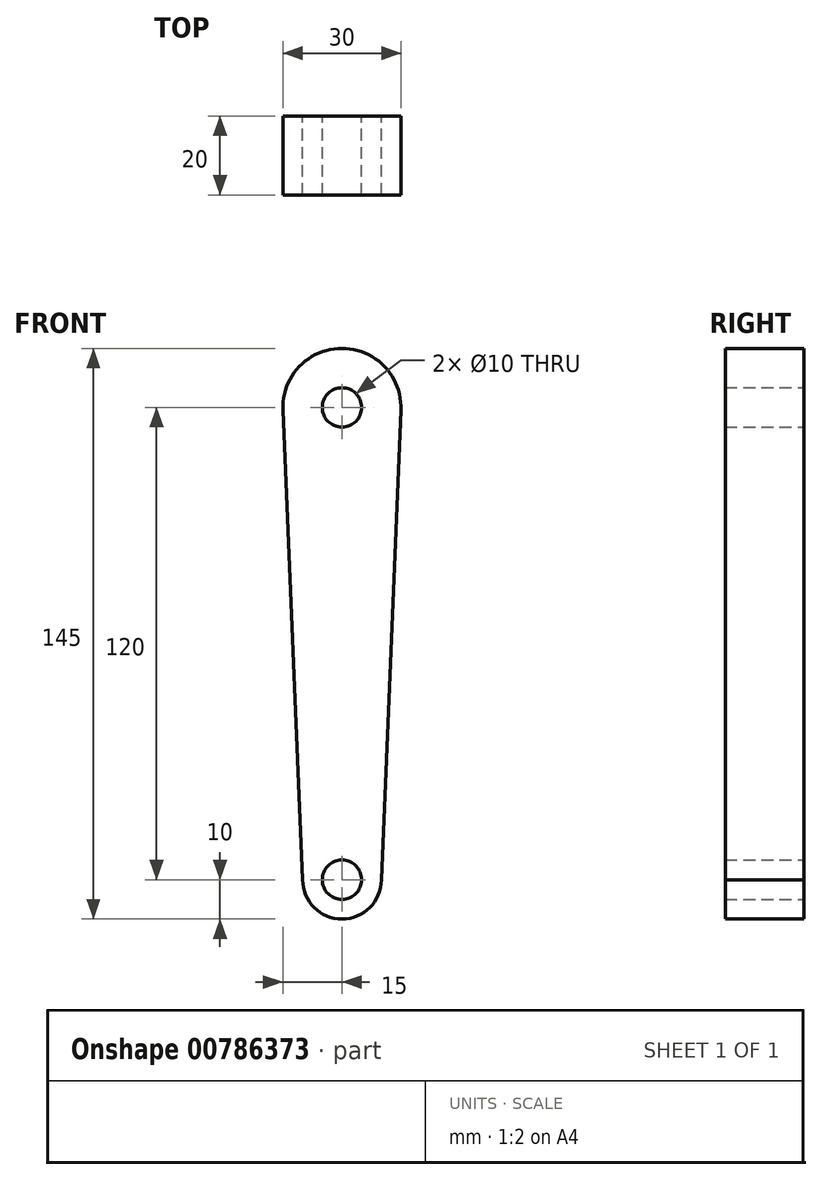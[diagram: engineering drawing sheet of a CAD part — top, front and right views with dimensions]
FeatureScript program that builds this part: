
annotation { "Feature Type Name" : "Feature", "Feature Type Description" : "" }
export const myFeature = defineFeature(function(context is Context, id is Id, definition is map)
    precondition{}
    {
        {
            var Q0;
            Q0=qCreatedBy(makeId("Front.planeOp"),FACE);
            var sketch = newSketch(context, id + "F0", { "sketchPlane" : qUnion([Q0])});
            skCircle(sketch, "E0", {"center": v(0, 0) * mm, "radius": 15 * mm});
            skCircle(sketch, "E1.0", {"center": v(0, 0) * mm, "radius": 5 * mm});
            skCircle(sketch, "E2", {"center": v(0, -120) * mm, "radius": 10 * mm});
            skLineSegment(sketch, "E3", {"start": v(-10, -120) * mm, "end": v(-14.99, -0.63) * mm});
            skLineSegment(sketch, "E4", {"start": v(10, -120) * mm, "end": v(14.99, -0.63) * mm});
            skCircle(sketch, "E5.0", {"center": v(0, -120) * mm, "radius": 5 * mm});
            skSolve(sketch);
        }
        {
            var Q0;
            {var subQ0=sQuery(id+"F0.wireOp",EDGE,"E3");Q0=makeQuery(id+"F0.imprint","IMPRINT",FACE,{"disambiguationData":[TD([[makeQuery(id+"F0.imprint","IMPRINT",EDGE,{"derivedFrom":subQ0}),-1.0]])]});}
            var Q1;
            Q1=makeQuery(id+"F0.imprint","IMPRINT",FACE,{"disambiguationData":[TD([[makeQuery(id+"F0.imprint","IMPRINT",EDGE,{"derivedFrom":sQuery(id+"F0.wireOp",EDGE,"E1.0")}),-1.0]])]});
            var Q2;
            Q2=makeQuery(id+"F0.imprint","IMPRINT",FACE,{"disambiguationData":[TD([[makeQuery(id+"F0.imprint","IMPRINT",EDGE,{"derivedFrom":sQuery(id+"F0.wireOp",EDGE,"E5.0")}),-1.0]])]});
            extrude(context, id + "F1", {"entities" : qUnion([Q0, Q1, Q2]), "depth" : 20 * mm, "offsetDistance" : 25 * mm});
        }
    });
